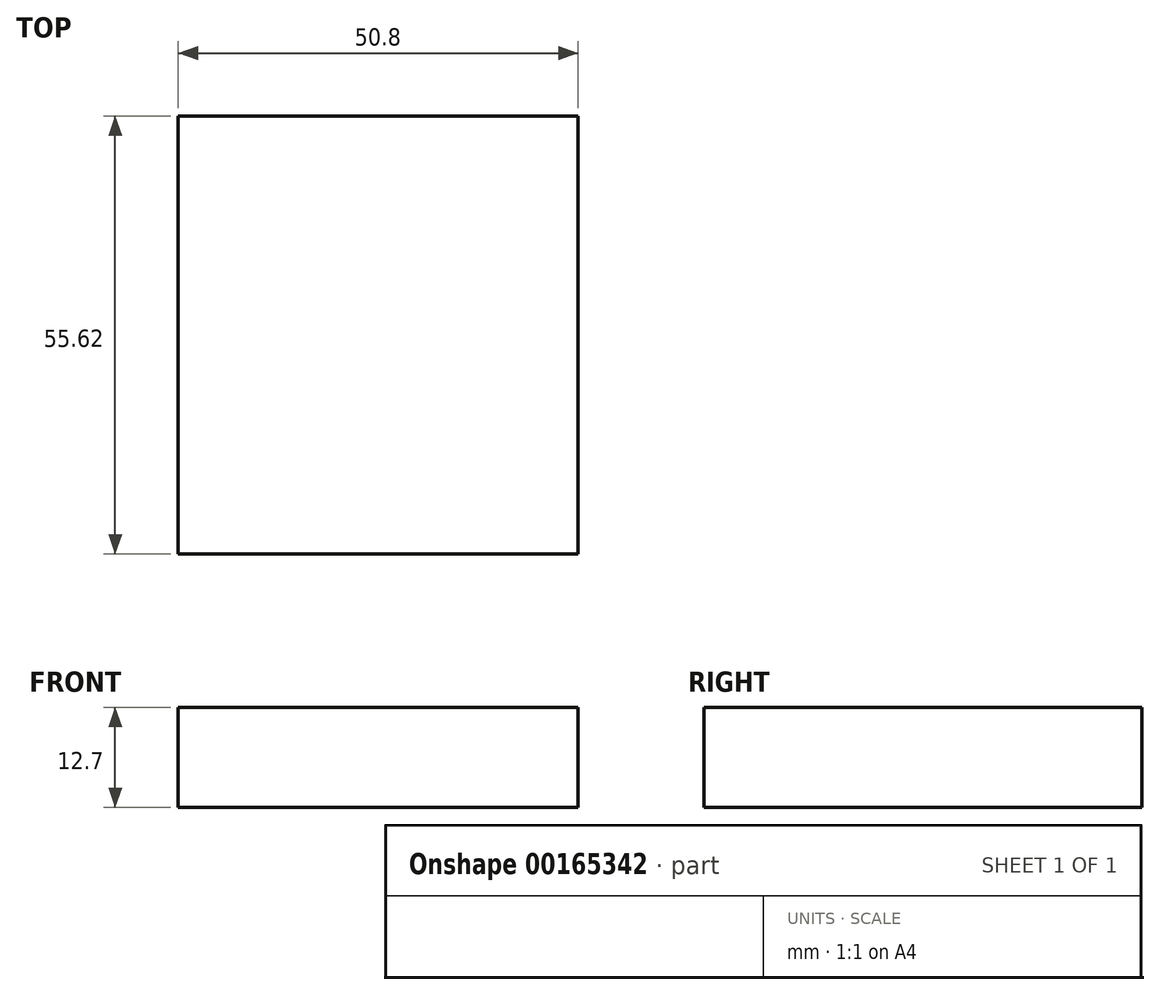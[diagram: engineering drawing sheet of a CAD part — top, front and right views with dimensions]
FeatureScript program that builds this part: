
annotation { "Feature Type Name" : "Feature", "Feature Type Description" : "" }
export const myFeature = defineFeature(function(context is Context, id is Id, definition is map)
    precondition{}
    {
        {
            var Q0;
            Q0=qCreatedBy(makeId("Top.planeOp"),FACE);
            var sketch = newSketch(context, id + "F0", { "sketchPlane" : qUnion([Q0])});
            skLineSegment(sketch, "E0.bottom", {"start": v(25.4, -27.81) * mm, "end": v(-25.4, -27.81) * mm});
            skLineSegment(sketch, "E0.top", {"start": v(25.4, 27.81) * mm, "end": v(-25.4, 27.81) * mm});
            skLineSegment(sketch, "E0.left", {"start": v(25.4, -27.81) * mm, "end": v(25.4, 27.81) * mm});
            skLineSegment(sketch, "E0.right", {"start": v(-25.4, -27.81) * mm, "end": v(-25.4, 27.81) * mm});
            skPoint(sketch, "E0.middle", {"position": v(0, 0) * mm});
            skSolve(sketch);
        }
        {
            var Q0;
            Q0=qSketchRegion(id+"F0",true);
            extrude(context, id + "F1", {"entities" : qUnion([Q0]), "depth" : 12.7 * mm});
        }
    });
